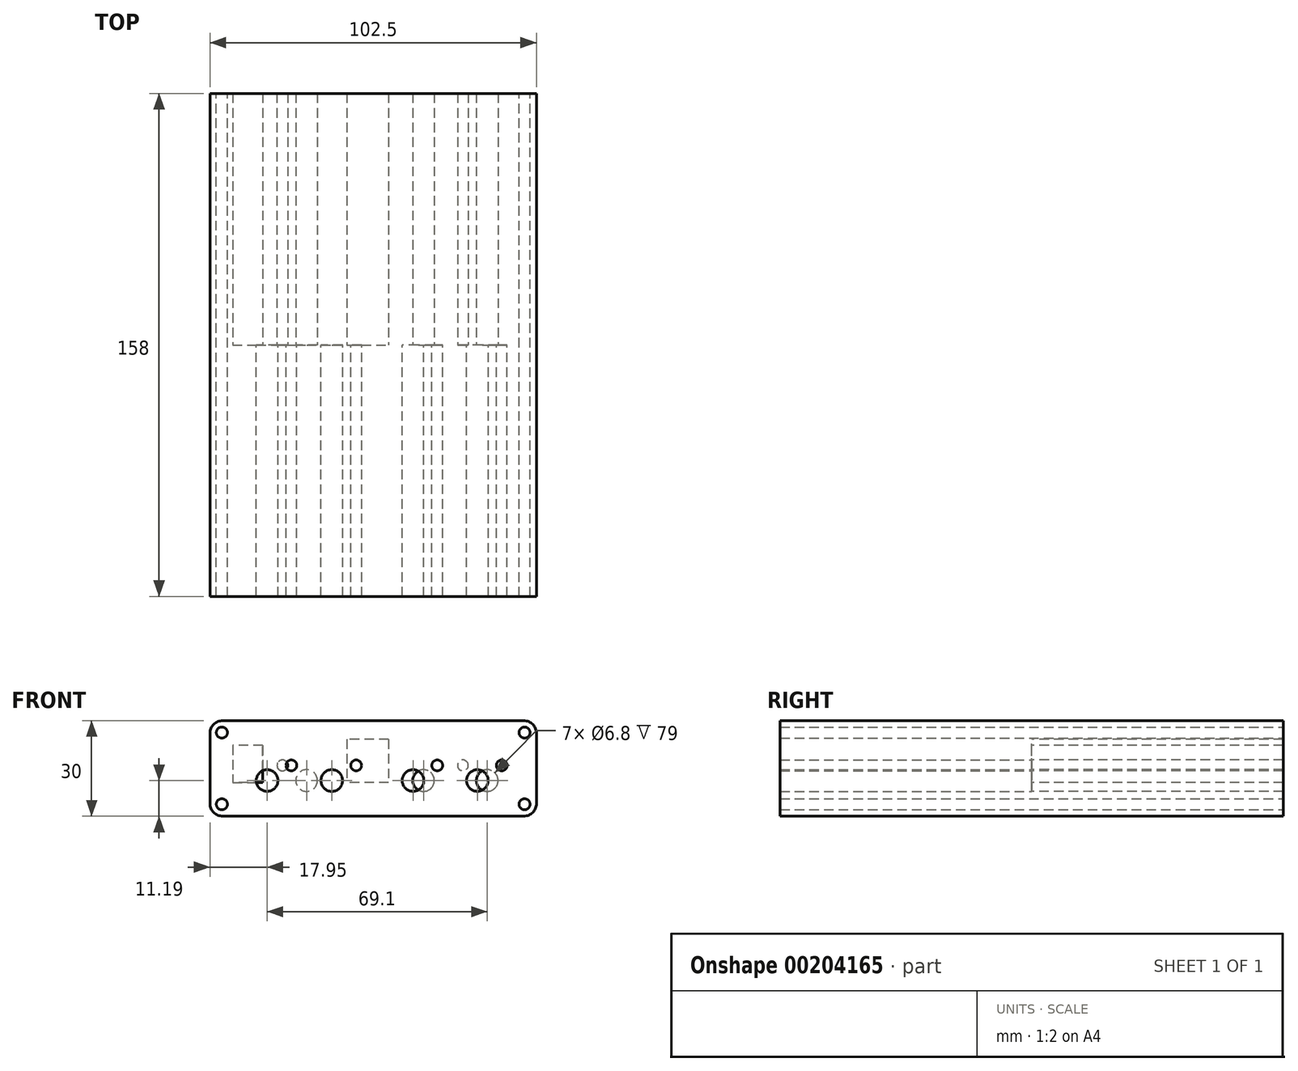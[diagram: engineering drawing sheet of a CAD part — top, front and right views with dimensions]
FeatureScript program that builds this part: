
annotation { "Feature Type Name" : "Feature", "Feature Type Description" : "" }
export const myFeature = defineFeature(function(context is Context, id is Id, definition is map)
    precondition{}
    {
        {
            var Q0;
            Q0=qCreatedBy(makeId("Front.planeOp"),FACE);
            var sketch = newSketch(context, id + "F0", { "sketchPlane" : qUnion([Q0])});
            skCircle(sketch, "E0", {"center": v(-33.3, 11.2) * mm, "radius": 3.4 * mm});
            skCircle(sketch, "E1", {"center": v(-13, 11.2) * mm, "radius": 3.4 * mm});
            skCircle(sketch, "E2", {"center": v(12.5, 11.2) * mm, "radius": 3.4 * mm});
            skCircle(sketch, "E3", {"center": v(32.7, 11.2) * mm, "radius": 3.4 * mm});
            skCircle(sketch, "E4", {"center": v(-25.7, 15.94) * mm, "radius": 1.7 * mm});
            skCircle(sketch, "E5", {"center": v(-5.35, 15.94) * mm, "radius": 1.7 * mm});
            skCircle(sketch, "E6", {"center": v(20.1, 15.94) * mm, "radius": 1.7 * mm});
            skCircle(sketch, "E7", {"center": v(40.35, 15.94) * mm, "radius": 1.7 * mm});
            skLineSegment(sketch, "E8", {"start": v(50, 52.6) * mm, "end": v(50, -49.51) * mm, "construction": true});
            skLineSegment(sketch, "E9.bottom", {"start": v(50, 10.8) * mm, "end": v(-50, 10.8) * mm, "construction": true});
            skLineSegment(sketch, "E9.top", {"start": v(50, 9.19) * mm, "end": v(-50, 9.2) * mm, "construction": true});
            skLineSegment(sketch, "E9.left", {"start": v(50, 10.8) * mm, "end": v(50, 9.2) * mm, "construction": true});
            skLineSegment(sketch, "E9.right", {"start": v(-50, 10.8) * mm, "end": v(-50, 9.2) * mm, "construction": true});
            skPoint(sketch, "E9.middle", {"position": v(0, 10) * mm});
            skSolve(sketch);
        }
        {
            var Q0;
            Q0=qCreatedBy(makeId("Front.planeOp"),FACE);
            var sketch = newSketch(context, id + "F1", { "sketchPlane" : qUnion([Q0])});
            skCircle(sketch, "E10", {"center": v(35.8, 11.2) * mm, "radius": 3.4 * mm});
            skCircle(sketch, "E11", {"center": v(15.8, 11.2) * mm, "radius": 3.4 * mm});
            skCircle(sketch, "E12", {"center": v(-20.9, 11.2) * mm, "radius": 3.4 * mm});
            skCircle(sketch, "E13", {"center": v(28.15, 15.94) * mm, "radius": 1.7 * mm});
            skCircle(sketch, "E14", {"center": v(-28.5, 15.94) * mm, "radius": 1.7 * mm});
            skLineSegment(sketch, "E15", {"start": v(50, 70.9) * mm, "end": v(50, -42.95) * mm, "construction": true});
            skLineSegment(sketch, "E16.bottom", {"start": v(50, 9.19) * mm, "end": v(-50, 9.2) * mm, "construction": true});
            skLineSegment(sketch, "E16.top", {"start": v(50, 10.79) * mm, "end": v(-50, 10.79) * mm, "construction": true});
            skLineSegment(sketch, "E16.left", {"start": v(50, 9.19) * mm, "end": v(50, 10.79) * mm, "construction": true});
            skLineSegment(sketch, "E16.right", {"start": v(-50, 9.2) * mm, "end": v(-50, 10.8) * mm, "construction": true});
            skPoint(sketch, "E16.middle", {"position": v(0, 9.99) * mm});
            skLineSegment(sketch, "E17.bottom", {"start": v(-8.25, 10.54) * mm, "end": v(4.85, 10.54) * mm});
            skLineSegment(sketch, "E17.top", {"start": v(-8.25, 24.14) * mm, "end": v(4.85, 24.14) * mm});
            skLineSegment(sketch, "E17.left", {"start": v(-8.25, 10.54) * mm, "end": v(-8.25, 24.14) * mm});
            skLineSegment(sketch, "E17.right", {"start": v(4.85, 10.54) * mm, "end": v(4.85, 24.14) * mm});
            skPoint(sketch, "E17.middle", {"position": v(-1.7, 17.34) * mm});
            skLineSegment(sketch, "E18.bottom", {"start": v(-44.15, 10.54) * mm, "end": v(-34.65, 10.54) * mm});
            skLineSegment(sketch, "E18.top", {"start": v(-44.15, 22.24) * mm, "end": v(-34.65, 22.24) * mm});
            skLineSegment(sketch, "E18.left", {"start": v(-44.15, 10.54) * mm, "end": v(-44.15, 22.24) * mm});
            skLineSegment(sketch, "E18.right", {"start": v(-34.65, 10.54) * mm, "end": v(-34.65, 22.24) * mm});
            skPoint(sketch, "E18.middle", {"position": v(-39.4, 16.4) * mm});
            skSolve(sketch);
        }
        {
            var Q0;
            Q0=qCreatedBy(makeId("Front.planeOp"),FACE);
            var sketch = newSketch(context, id + "F2", { "sketchPlane" : qUnion([Q0])});
            skLineSegment(sketch, "E19.bottom", {"start": v(47.25, 0) * mm, "end": v(-47.25, 0) * mm});
            skLineSegment(sketch, "E19.top", {"start": v(47.25, 30) * mm, "end": v(-47.25, 30) * mm});
            skLineSegment(sketch, "E19.left", {"start": v(51.25, 4) * mm, "end": v(51.25, 26) * mm});
            skLineSegment(sketch, "E19.right", {"start": v(-51.25, 4) * mm, "end": v(-51.25, 26) * mm});
            skPoint(sketch, "E19.middle", {"position": v(0, 15) * mm});
            skLineSegment(sketch, "E20.bottom", {"start": v(-47.5, 3.74) * mm, "end": v(47.51, 3.74) * mm, "construction": true});
            skLineSegment(sketch, "E20.top", {"start": v(-47.51, 26.26) * mm, "end": v(47.51, 26.26) * mm, "construction": true});
            skLineSegment(sketch, "E20.left", {"start": v(-47.51, 3.74) * mm, "end": v(-47.51, 26.26) * mm, "construction": true});
            skLineSegment(sketch, "E20.right", {"start": v(47.51, 3.74) * mm, "end": v(47.51, 26.26) * mm, "construction": true});
            skCircle(sketch, "E21", {"center": v(47.51, 26.26) * mm, "radius": 1.75 * mm});
            skCircle(sketch, "E22", {"center": v(-47.51, 26.26) * mm, "radius": 1.75 * mm});
            skCircle(sketch, "E23", {"center": v(-47.5, 3.74) * mm, "radius": 1.75 * mm});
            skCircle(sketch, "E24", {"center": v(47.51, 3.74) * mm, "radius": 1.75 * mm});
            skPoint(sketch, "E25.visualSharp", {"position": v(51.25, 30) * mm});
            skArc(sketch, "E25.filletArc", {"start": v(51.25, 26) * mm, "mid": v(50.08, 28.83) * mm, "end": v(47.25, 30) * mm});
            skPoint(sketch, "E26.visualSharp", {"position": v(-51.25, 30) * mm});
            skArc(sketch, "E26.filletArc", {"start": v(-47.25, 30) * mm, "mid": v(-50.08, 28.83) * mm, "end": v(-51.25, 26) * mm});
            skPoint(sketch, "E27.visualSharp", {"position": v(-51.25, 0) * mm});
            skArc(sketch, "E27.filletArc", {"start": v(-51.25, 4) * mm, "mid": v(-50.08, 1.17) * mm, "end": v(-47.25, 0) * mm});
            skPoint(sketch, "E28.visualSharp", {"position": v(51.25, 0) * mm});
            skArc(sketch, "E28.filletArc", {"start": v(47.25, 0) * mm, "mid": v(50.08, 1.17) * mm, "end": v(51.25, 4) * mm});
            skSolve(sketch);
        }
        {
            var Q0;
            Q0 = qSketchRegion(id + "F2", true);
            extrude(context, id + "F3", {"entities" : qUnion([Q0]), "endBound" : BoundingType.SYMMETRIC, "depth" : (160 + 2 * 3 - 8) * mm});
        }
        {
            var Q0;
            Q0 = qSketchRegion(id + "F0", true);
            var Q1;
            Q1=makeQuery(id+"F3.opExtrude","CAP_FACE",FACE,{"disambiguationData":[OSD([sQuery(id+"F2.wireOp",EDGE,"E19.bottom"),sQuery(id+"F2.wireOp",EDGE,"E19.top"),sQuery(id+"F2.wireOp",EDGE,"E19.left"),sQuery(id+"F2.wireOp",EDGE,"E19.right"),sQuery(id+"F2.wireOp",EDGE,"E21"),sQuery(id+"F2.wireOp",EDGE,"E22"),sQuery(id+"F2.wireOp",EDGE,"E23"),sQuery(id+"F2.wireOp",EDGE,"E24"),sQuery(id+"F2.wireOp",EDGE,"E25.filletArc"),sQuery(id+"F2.wireOp",EDGE,"E26.filletArc"),sQuery(id+"F2.wireOp",EDGE,"E27.filletArc"),sQuery(id+"F2.wireOp",EDGE,"E28.filletArc")])],"isStart":false});
            extrude(context, id + "F4", {"entities" : qUnion([Q0]), "operationType" : NewBodyOperationType.REMOVE, "endBound" : BoundingType.UP_TO_SURFACE, "endBoundEntityFace" : qUnion([Q1]), "depth" : 25 * mm});
        }
        {
            var Q0;
            Q0 = qSketchRegion(id + "F1", true);
            var Q1;
            Q1=makeQuery(id+"F3.opExtrude","CAP_FACE",FACE,{"disambiguationData":[OSD([sQuery(id+"F2.wireOp",EDGE,"E19.bottom"),sQuery(id+"F2.wireOp",EDGE,"E19.top"),sQuery(id+"F2.wireOp",EDGE,"E19.left"),sQuery(id+"F2.wireOp",EDGE,"E19.right"),sQuery(id+"F2.wireOp",EDGE,"E21"),sQuery(id+"F2.wireOp",EDGE,"E22"),sQuery(id+"F2.wireOp",EDGE,"E23"),sQuery(id+"F2.wireOp",EDGE,"E24"),sQuery(id+"F2.wireOp",EDGE,"E25.filletArc"),sQuery(id+"F2.wireOp",EDGE,"E26.filletArc"),sQuery(id+"F2.wireOp",EDGE,"E27.filletArc"),sQuery(id+"F2.wireOp",EDGE,"E28.filletArc")])],"isStart":true});
            extrude(context, id + "F5", {"entities" : qUnion([Q0]), "operationType" : NewBodyOperationType.REMOVE, "endBound" : BoundingType.UP_TO_SURFACE, "oppositeDirection" : true, "endBoundEntityFace" : qUnion([Q1]), "depth" : 25 * mm});
        }
    });
